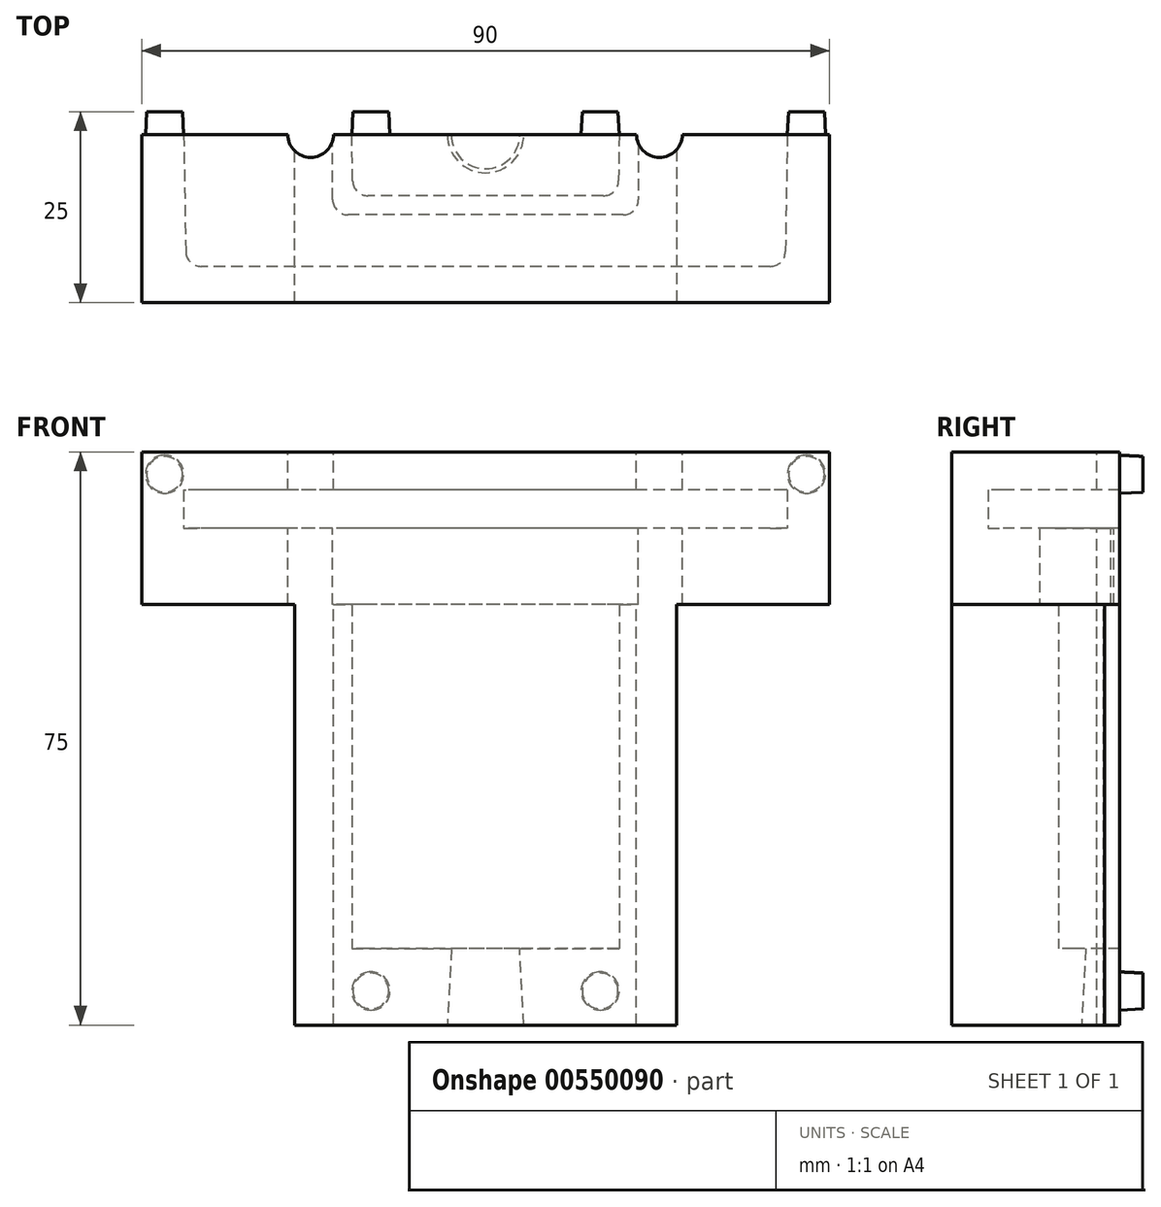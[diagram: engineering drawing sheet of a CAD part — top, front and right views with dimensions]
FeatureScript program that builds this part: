
annotation { "Feature Type Name" : "Feature", "Feature Type Description" : "" }
export const myFeature = defineFeature(function(context is Context, id is Id, definition is map)
    precondition{}
    {
        {
            var Q0;
            Q0=qCreatedBy(makeId("Top.planeOp"),FACE);
            var sketch = newSketch(context, id + "F0", { "sketchPlane" : qUnion([Q0])});
            skLineSegment(sketch, "E0.bottom", {"start": v(45, -44.53) * mm, "end": v(-45, -44.53) * mm});
            skLineSegment(sketch, "E0.top", {"start": v(45, -66.53) * mm, "end": v(-45, -66.53) * mm});
            skLineSegment(sketch, "E0.left", {"start": v(45, -44.53) * mm, "end": v(45, -66.53) * mm});
            skLineSegment(sketch, "E0.right", {"start": v(-45, -44.53) * mm, "end": v(-45, -66.53) * mm});
            skPoint(sketch, "E0.middle", {"position": v(0, -55.53) * mm});
            skSolve(sketch);
        }
        {
            var Q0;
            Q0 = qSketchRegion(id + "F0", true);
            extrude(context, id + "F1", {"entities" : qUnion([Q0]), "depth" : 10 * mm, "offsetDistance" : 25 * mm});
        }
        {
            var Q0;
            Q0=makeQuery(id+"F1.opExtrude","CAP_FACE",FACE,{"disambiguationData":[OSD([sQuery(id+"F0.wireOp",EDGE,"E0.bottom"),sQuery(id+"F0.wireOp",EDGE,"E0.top"),sQuery(id+"F0.wireOp",EDGE,"E0.left"),sQuery(id+"F0.wireOp",EDGE,"E0.right")])],"isStart":true});
            var sketch = newSketch(context, id + "F2", { "sketchPlane" : qUnion([Q0])});
            skLineSegment(sketch, "E1", {"start": v(0, 44.53) * mm, "end": v(39.5, 44.53) * mm});
            skLineSegment(sketch, "E2", {"start": v(39.5, 44.53) * mm, "end": v(39.5, 61.78) * mm});
            skLineSegment(sketch, "E3", {"start": v(39.5, 61.78) * mm, "end": v(-39.5, 61.78) * mm});
            skLineSegment(sketch, "E4", {"start": v(-39.5, 61.78) * mm, "end": v(-39.5, 44.53) * mm});
            skLineSegment(sketch, "E5", {"start": v(-39.5, 44.53) * mm, "end": v(0, 44.53) * mm});
            skLineSegment(sketch, "E6", {"start": v(-39.5, 44.53) * mm, "end": v(-39.2, 61.78) * mm});
            skLineSegment(sketch, "E7", {"start": v(39.5, 44.53) * mm, "end": v(39.2, 61.78) * mm});
            skSolve(sketch);
        }
        {
            var Q0;
            Q0=makeQuery(id+"F2.imprint","IMPRINT",FACE,{"disambiguationData":[TD([[makeQuery(id+"F2.imprint","IMPRINT",EDGE,{"derivedFrom":sQuery(id+"F2.wireOp",EDGE,"E1")}),-1.0]])]});
            extrude(context, id + "F3", {"entities" : qUnion([Q0]), "operationType" : NewBodyOperationType.REMOVE, "oppositeDirection" : true, "depth" : 5 * mm, "offsetDistance" : 25 * mm});
        }
        {
            var Q0;
            Q0=makeQuery(id+"F3.boolean.opBoolean","COPY",EDGE,{"derivedFrom":makeQuery(id+"F3.opExtrude","SWEPT_EDGE",EDGE,{"disambiguationData":[OSD([sQuery(id+"F2.wireOp",EDGE,"E3"),sQuery(id+"F2.wireOp",EDGE,"E6")])]})});
            var Q1;
            Q1=makeQuery(id+"F3.boolean.opBoolean","COPY",EDGE,{"derivedFrom":makeQuery(id+"F3.opExtrude","SWEPT_EDGE",EDGE,{"disambiguationData":[OSD([sQuery(id+"F2.wireOp",EDGE,"E3"),sQuery(id+"F2.wireOp",EDGE,"E7")])]})});
            fillet(context, id + "F4", {"entities" : qUnion([Q0, Q1]), "radius" : 2 * mm, "tangentPropagation" : true, "allowEdgeOverflow" : false});
        }
        {
            var Q0;
            Q0=makeQuery(id+"F1.opExtrude","CAP_FACE",FACE,{"disambiguationData":[OSD([sQuery(id+"F0.wireOp",EDGE,"E0.bottom"),sQuery(id+"F0.wireOp",EDGE,"E0.top"),sQuery(id+"F0.wireOp",EDGE,"E0.left"),sQuery(id+"F0.wireOp",EDGE,"E0.right")])],"isStart":true});
            var sketch = newSketch(context, id + "F5", { "sketchPlane" : qUnion([Q0])});
            skLineSegment(sketch, "E8", {"start": v(-45, 44.53) * mm, "end": v(45, 44.53) * mm});
            skLineSegment(sketch, "E9", {"start": v(45, 44.53) * mm, "end": v(45, 66.53) * mm});
            skLineSegment(sketch, "E10", {"start": v(45, 66.53) * mm, "end": v(-45, 66.53) * mm});
            skLineSegment(sketch, "E11", {"start": v(-45, 66.53) * mm, "end": v(-45, 44.53) * mm});
            skSolve(sketch);
        }
        {
            var Q0;
            Q0 = qSketchRegion(id + "F5", true);
            extrude(context, id + "F6", {"entities" : qUnion([Q0]), "operationType" : NewBodyOperationType.ADD, "depth" : 10 * mm, "offsetDistance" : 25 * mm});
        }
        {
            var Q0;
            Q0=makeQuery(id+"F6.opExtrude","CAP_FACE",FACE,{"disambiguationData":[OSD([sQuery(id+"F5.wireOp",EDGE,"E8"),sQuery(id+"F5.wireOp",EDGE,"E9"),sQuery(id+"F5.wireOp",EDGE,"E10"),sQuery(id+"F5.wireOp",EDGE,"E11")])],"isStart":false});
            var sketch = newSketch(context, id + "F7", { "sketchPlane" : qUnion([Q0])});
            skLineSegment(sketch, "E12", {"start": v(0, 44.53) * mm, "end": v(20, 44.53) * mm});
            skLineSegment(sketch, "E13", {"start": v(20, 44.53) * mm, "end": v(20, 55.03) * mm});
            skLineSegment(sketch, "E14", {"start": v(20, 55.03) * mm, "end": v(-20, 55.03) * mm});
            skLineSegment(sketch, "E15", {"start": v(-20, 55.03) * mm, "end": v(-20, 44.53) * mm});
            skLineSegment(sketch, "E16", {"start": v(-20, 44.53) * mm, "end": v(0, 44.53) * mm});
            skLineSegment(sketch, "E17", {"start": v(-20, 44.53) * mm, "end": v(-19.82, 55.03) * mm});
            skLineSegment(sketch, "E18", {"start": v(20, 44.53) * mm, "end": v(19.82, 55.03) * mm});
            skSolve(sketch);
        }
        {
            var Q0;
            Q0 = qSketchRegion(id + "F7", true);
            var Q1;
            Q1=makeQuery(id+"F7.imprint","IMPRINT",FACE,{"disambiguationData":[TD([[makeQuery(id+"F7.imprint","IMPRINT",EDGE,{"derivedFrom":sQuery(id+"F7.wireOp",EDGE,"E12")}),-1.0]])]});
            extrude(context, id + "F8", {"entities" : qUnion([Q0, Q1]), "operationType" : NewBodyOperationType.REMOVE, "oppositeDirection" : true, "depth" : 10 * mm, "offsetDistance" : 25 * mm});
        }
        {
            var Q0;
            Q0=makeQuery(id+"F8.boolean.opBoolean","COPY",EDGE,{"derivedFrom":makeQuery(id+"F8.opExtrude","SWEPT_EDGE",EDGE,{"disambiguationData":[OSD([sQuery(id+"F7.wireOp",EDGE,"E14"),sQuery(id+"F7.wireOp",EDGE,"E15")])]})});
            var Q1;
            Q1=makeQuery(id+"F8.boolean.opBoolean","COPY",EDGE,{"derivedFrom":makeQuery(id+"F8.opExtrude","SWEPT_EDGE",EDGE,{"disambiguationData":[OSD([sQuery(id+"F7.wireOp",EDGE,"E13"),sQuery(id+"F7.wireOp",EDGE,"E14")])]})});
            fillet(context, id + "F9", {"entities" : qUnion([Q0, Q1]), "radius" : 2 * mm, "tangentPropagation" : true, "allowEdgeOverflow" : false});
        }
        {
            var Q0;
            Q0=makeQuery(id+"F6.opExtrude","CAP_FACE",FACE,{"disambiguationData":[OSD([sQuery(id+"F5.wireOp",EDGE,"E8"),sQuery(id+"F5.wireOp",EDGE,"E9"),sQuery(id+"F5.wireOp",EDGE,"E10"),sQuery(id+"F5.wireOp",EDGE,"E11")])],"isStart":false});
            var sketch = newSketch(context, id + "F10", { "sketchPlane" : qUnion([Q0])});
            skLineSegment(sketch, "E19", {"start": v(0, 44.53) * mm, "end": v(25, 44.53) * mm});
            skLineSegment(sketch, "E20", {"start": v(25, 44.53) * mm, "end": v(25, 66.53) * mm});
            skLineSegment(sketch, "E21", {"start": v(25, 66.53) * mm, "end": v(-25, 66.53) * mm});
            skLineSegment(sketch, "E22", {"start": v(-25, 66.53) * mm, "end": v(-25, 44.53) * mm});
            skLineSegment(sketch, "E23", {"start": v(-25, 44.53) * mm, "end": v(0, 44.53) * mm});
            skSolve(sketch);
        }
        {
            var Q0;
            Q0 = qSketchRegion(id + "F10", true);
            extrude(context, id + "F11", {"entities" : qUnion([Q0]), "operationType" : NewBodyOperationType.ADD, "depth" : 45 * mm, "offsetDistance" : 25 * mm});
        }
        {
            var Q0;
            Q0=makeQuery(id+"F11.opExtrude","CAP_FACE",FACE,{"disambiguationData":[OSD([sQuery(id+"F10.wireOp",EDGE,"E19"),sQuery(id+"F10.wireOp",EDGE,"E20"),sQuery(id+"F10.wireOp",EDGE,"E21"),sQuery(id+"F10.wireOp",EDGE,"E22"),sQuery(id+"F10.wireOp",EDGE,"E23")])],"isStart":false});
            var sketch = newSketch(context, id + "F12", { "sketchPlane" : qUnion([Q0])});
            skLineSegment(sketch, "E24", {"start": v(0, 44.53) * mm, "end": v(17.5, 44.53) * mm});
            skLineSegment(sketch, "E25", {"start": v(17.5, 44.53) * mm, "end": v(17.5, 52.53) * mm});
            skLineSegment(sketch, "E26", {"start": v(17.5, 52.53) * mm, "end": v(-17.5, 52.53) * mm});
            skLineSegment(sketch, "E27", {"start": v(-17.5, 52.53) * mm, "end": v(-17.5, 44.53) * mm});
            skLineSegment(sketch, "E28", {"start": v(-17.5, 44.53) * mm, "end": v(0, 44.53) * mm});
            skLineSegment(sketch, "E29", {"start": v(-17.36, 52.53) * mm, "end": v(-17.5, 44.53) * mm});
            skLineSegment(sketch, "E30", {"start": v(17.5, 44.53) * mm, "end": v(17.36, 52.53) * mm});
            skSolve(sketch);
        }
        {
            var Q0;
            Q0=makeQuery(id+"F12.imprint","IMPRINT",FACE,{"disambiguationData":[TD([[makeQuery(id+"F12.imprint","IMPRINT",EDGE,{"derivedFrom":sQuery(id+"F12.wireOp",EDGE,"E24")}),1.0]])]});
            extrude(context, id + "F13", {"entities" : qUnion([Q0]), "operationType" : NewBodyOperationType.REMOVE, "oppositeDirection" : true, "depth" : 45 * mm, "offsetDistance" : 25 * mm});
        }
        {
            var Q0;
            Q0=makeQuery(id+"F13.boolean.opBoolean","COPY",EDGE,{"derivedFrom":makeQuery(id+"F13.opExtrude","SWEPT_EDGE",EDGE,{"disambiguationData":[OSD([sQuery(id+"F12.wireOp",EDGE,"E26"),sQuery(id+"F12.wireOp",EDGE,"E29")])]})});
            var Q1;
            Q1=makeQuery(id+"F13.boolean.opBoolean","COPY",EDGE,{"derivedFrom":makeQuery(id+"F13.opExtrude","SWEPT_EDGE",EDGE,{"disambiguationData":[OSD([sQuery(id+"F12.wireOp",EDGE,"E26"),sQuery(id+"F12.wireOp",EDGE,"E30")])]})});
            fillet(context, id + "F14", {"entities" : qUnion([Q0, Q1]), "radius" : 2 * mm, "tangentPropagation" : true, "allowEdgeOverflow" : false});
        }
        {
            var Q0;
            Q0=makeQuery(id+"F11.opExtrude","CAP_FACE",FACE,{"disambiguationData":[OSD([sQuery(id+"F10.wireOp",EDGE,"E19"),sQuery(id+"F10.wireOp",EDGE,"E20"),sQuery(id+"F10.wireOp",EDGE,"E21"),sQuery(id+"F10.wireOp",EDGE,"E22"),sQuery(id+"F10.wireOp",EDGE,"E23")])],"isStart":false});
            var sketch = newSketch(context, id + "F15", { "sketchPlane" : qUnion([Q0])});
            skLineSegment(sketch, "E31.bottom", {"start": v(-25, 66.53) * mm, "end": v(25, 66.53) * mm});
            skLineSegment(sketch, "E31.top", {"start": v(-25, 44.53) * mm, "end": v(25, 44.53) * mm});
            skLineSegment(sketch, "E31.left", {"start": v(-25, 66.53) * mm, "end": v(-25, 44.53) * mm});
            skLineSegment(sketch, "E31.right", {"start": v(25, 66.53) * mm, "end": v(25, 44.53) * mm});
            skSolve(sketch);
        }
        {
            var Q0;
            Q0 = qSketchRegion(id + "F15", true);
            extrude(context, id + "F16", {"entities" : qUnion([Q0]), "operationType" : NewBodyOperationType.ADD, "depth" : 10 * mm, "offsetDistance" : 25 * mm});
        }
        {
            var Q0;
            Q0=makeQuery(id+"F16.opExtrude","CAP_FACE",FACE,{"disambiguationData":[OSD([sQuery(id+"F15.wireOp",EDGE,"E31.bottom"),sQuery(id+"F15.wireOp",EDGE,"E31.top"),sQuery(id+"F15.wireOp",EDGE,"E31.left"),sQuery(id+"F15.wireOp",EDGE,"E31.right")])],"isStart":false});
            var sketch = newSketch(context, id + "F17", { "sketchPlane" : qUnion([Q0])});
            skCircle(sketch, "E32", {"center": v(0, 44.53) * mm, "radius": 5 * mm});
            skSolve(sketch);
        }
        {
            var Q0;
            Q0 = qSketchRegion(id + "F17", true);
            extrude(context, id + "F18", {"entities" : qUnion([Q0]), "operationType" : NewBodyOperationType.REMOVE, "oppositeDirection" : true, "depth" : 25 * mm, "offsetDistance" : 25 * mm, "hasDraft" : true, "draftAngle" : 3 * degree, "draftPullDirection" : true});
        }
        {
            var Q0;
            Q0=makeQuery(id+"F1.opExtrude","CAP_FACE",FACE,{"disambiguationData":[OSD([sQuery(id+"F0.wireOp",EDGE,"E0.bottom"),sQuery(id+"F0.wireOp",EDGE,"E0.top"),sQuery(id+"F0.wireOp",EDGE,"E0.left"),sQuery(id+"F0.wireOp",EDGE,"E0.right")])],"isStart":false});
            var sketch = newSketch(context, id + "F19", { "sketchPlane" : qUnion([Q0])});
            skLineSegment(sketch, "E33", {"start": v(0, -44.53) * mm, "end": v(22.8, -44.53) * mm});
            skLineSegment(sketch, "E34", {"start": v(0, -44.53) * mm, "end": v(-22.8, -44.53) * mm});
            skSolve(sketch);
        }
        {
            var Q0;
            {var subQ2=sQuery(id+"F19.wireOp",EDGE,"E33");Q0=makeQuery(id+"F19.imprint","IMPRINT",FACE,{"disambiguationData":[TD([[makeQuery(id+"F19.imprint","IMPRINT",EDGE,{"derivedFrom":subQ2}),1.0]])]});}
            var sketch = newSketch(context, id + "F20", { "sketchPlane" : qUnion([Q0])});
            skCircle(sketch, "E35", {"center": v(22.75, -44.52) * mm, "radius": 3 * mm});
            skCircle(sketch, "E36", {"center": v(-22.89, -44.52) * mm, "radius": 3 * mm});
            skSolve(sketch);
        }
        {
            var Q0;
            Q0 = qSketchRegion(id + "F20", true);
            extrude(context, id + "F21", {"entities" : qUnion([Q0]), "operationType" : NewBodyOperationType.REMOVE, "oppositeDirection" : true, "depth" : 90 * mm, "offsetDistance" : 25 * mm});
        }
        {
            var Q0;
            {var subQ0=sQuery(id+"F15.wireOp",EDGE,"E31.right");var subQ1=sQuery(id+"F15.wireOp",EDGE,"E31.left");var subQ2=sQuery(id+"F15.wireOp",EDGE,"E31.top");var subQ3=sQuery(id+"F15.wireOp",EDGE,"E31.bottom");var subQ4=sQuery(id+"F10.wireOp",EDGE,"E23");var subQ5=sQuery(id+"F10.wireOp",EDGE,"E19");Q0=makeQuery(id+"F21.boolean.opBoolean","SPLIT",FACE,{"disambiguationData":[TD([makeQuery(id+"F11.opExtrude","CAP_FACE",FACE,{"disambiguationData":[OSD([subQ5,sQuery(id+"F10.wireOp",EDGE,"E20"),sQuery(id+"F10.wireOp",EDGE,"E21"),sQuery(id+"F10.wireOp",EDGE,"E22"),subQ4])],"isStart":true}),makeQuery(id+"F13.boolean.opBoolean","COPY",FACE,{"derivedFrom":makeQuery(id+"F13.opExtrude","SWEPT_FACE",FACE,{"disambiguationData":[OSD([sQuery(id+"F12.wireOp",EDGE,"E30")])]})}),makeQuery(id+"F16.opExtrude","CAP_FACE",FACE,{"disambiguationData":[OSD([subQ3,subQ2,subQ1,subQ0])],"isStart":true}),makeQuery(id+"F16.opExtrude","CAP_FACE",FACE,{"disambiguationData":[OSD([subQ3,subQ2,subQ1,subQ0])],"isStart":false}),makeQuery(id+"F18.boolean.opBoolean","COPY",FACE,{"derivedFrom":makeQuery(id+"F18.opExtrude","SWEPT_FACE",FACE,{"disambiguationData":[OSD([sQuery(id+"F17.wireOp",EDGE,"E32")])]})}),makeQuery(id+"F21.opExtrude","SWEPT_FACE",FACE,{"disambiguationData":[OSD([sQuery(id+"F20.wireOp",EDGE,"E35")])]})])],"derivedFrom":makeQuery(id+"F16.boolean.opBoolean","MERGE",FACE,{"derivedFrom":[makeQuery(id+"F11.boolean.opBoolean","MERGE",FACE,{"derivedFrom":[makeQuery(id+"F6.boolean.opBoolean","MERGE",FACE,{"derivedFrom":[makeQuery(id+"F1.opExtrude","SWEPT_FACE",FACE,{"disambiguationData":[OSD([sQuery(id+"F0.wireOp",EDGE,"E0.bottom")])]}),makeQuery(id+"F6.opExtrude","SWEPT_FACE",FACE,{"disambiguationData":[OSD([sQuery(id+"F5.wireOp",EDGE,"E8")])]})]}),makeQuery(id+"F11.opExtrude","SWEPT_FACE",FACE,{"disambiguationData":[OSD([subQ5,subQ4])]})]}),makeQuery(id+"F16.opExtrude","SWEPT_FACE",FACE,{"disambiguationData":[OSD([subQ2])]})]})});}
            var sketch = newSketch(context, id + "F22", { "sketchPlane" : qUnion([Q0])});
            skCircle(sketch, "E37", {"center": v(-15, -60.54) * mm, "radius": 2.5 * mm});
            skCircle(sketch, "E38.MirrorC", {"center": v(15, -60.54) * mm, "radius": 2.5 * mm});
            skSolve(sketch);
        }
        {
            var Q0;
            Q0 = qSketchRegion(id + "F22", true);
            extrude(context, id + "F23", {"entities" : qUnion([Q0]), "operationType" : NewBodyOperationType.ADD, "depth" : 3 * mm, "offsetDistance" : 25 * mm, "hasDraft" : true, "draftAngle" : 3 * degree, "draftPullDirection" : true});
        }
        {
            var Q0;
            {var subQ0=sQuery(id+"F2.wireOp",EDGE,"E7");var subQ1=sQuery(id+"F0.wireOp",EDGE,"E0.left");var subQ2=sQuery(id+"F0.wireOp",EDGE,"E0.bottom");var subQ3=sQuery(id+"F5.wireOp",EDGE,"E9");var subQ4=sQuery(id+"F5.wireOp",EDGE,"E11");var subQ5=sQuery(id+"F5.wireOp",EDGE,"E10");var subQ6=sQuery(id+"F5.wireOp",EDGE,"E8");Q0=makeQuery(id+"F21.boolean.opBoolean","SPLIT",FACE,{"disambiguationData":[TD([makeQuery(id+"F1.opExtrude","CAP_FACE",FACE,{"disambiguationData":[OSD([subQ2,sQuery(id+"F0.wireOp",EDGE,"E0.top"),subQ1,sQuery(id+"F0.wireOp",EDGE,"E0.right")])],"isStart":false}),makeQuery(id+"F1.opExtrude","SWEPT_FACE",FACE,{"disambiguationData":[OSD([subQ1])]}),makeQuery(id+"F3.boolean.opBoolean","COPY",FACE,{"derivedFrom":makeQuery(id+"F3.opExtrude","CAP_FACE",FACE,{"disambiguationData":[OSD([sQuery(id+"F2.wireOp",EDGE,"E1"),sQuery(id+"F2.wireOp",EDGE,"E3"),sQuery(id+"F2.wireOp",EDGE,"E5"),sQuery(id+"F2.wireOp",EDGE,"E6"),subQ0])],"isStart":false})}),makeQuery(id+"F3.boolean.opBoolean","COPY",FACE,{"derivedFrom":makeQuery(id+"F3.opExtrude","SWEPT_FACE",FACE,{"disambiguationData":[OSD([subQ0])]})}),makeQuery(id+"F6.opExtrude","CAP_FACE",FACE,{"disambiguationData":[OSD([subQ6,subQ3,subQ5,subQ4])],"isStart":true}),makeQuery(id+"F6.opExtrude","CAP_FACE",FACE,{"disambiguationData":[OSD([subQ6,subQ3,subQ5,subQ4])],"isStart":false}),makeQuery(id+"F6.opExtrude","SWEPT_FACE",FACE,{"disambiguationData":[OSD([subQ3])]}),makeQuery(id+"F21.opExtrude","SWEPT_FACE",FACE,{"disambiguationData":[OSD([sQuery(id+"F20.wireOp",EDGE,"E35")])]})])],"derivedFrom":makeQuery(id+"F16.boolean.opBoolean","MERGE",FACE,{"derivedFrom":[makeQuery(id+"F11.boolean.opBoolean","MERGE",FACE,{"derivedFrom":[makeQuery(id+"F6.boolean.opBoolean","MERGE",FACE,{"derivedFrom":[makeQuery(id+"F1.opExtrude","SWEPT_FACE",FACE,{"disambiguationData":[OSD([subQ2])]}),makeQuery(id+"F6.opExtrude","SWEPT_FACE",FACE,{"disambiguationData":[OSD([subQ6])]})]}),makeQuery(id+"F11.opExtrude","SWEPT_FACE",FACE,{"disambiguationData":[OSD([sQuery(id+"F10.wireOp",EDGE,"E19"),sQuery(id+"F10.wireOp",EDGE,"E23")])]})]}),makeQuery(id+"F16.opExtrude","SWEPT_FACE",FACE,{"disambiguationData":[OSD([sQuery(id+"F15.wireOp",EDGE,"E31.top")])]})]})});}
            var sketch = newSketch(context, id + "F24", { "sketchPlane" : qUnion([Q0])});
            skCircle(sketch, "E39", {"center": v(-42, 7.06) * mm, "radius": 2.5 * mm});
            skCircle(sketch, "E40.MirrorC", {"center": v(42, 7.06) * mm, "radius": 2.5 * mm});
            skSolve(sketch);
        }
        {
            var Q0;
            Q0 = qSketchRegion(id + "F24", true);
            extrude(context, id + "F25", {"entities" : qUnion([Q0]), "operationType" : NewBodyOperationType.ADD, "depth" : 3 * mm, "offsetDistance" : 25 * mm, "hasDraft" : true, "draftAngle" : 3 * degree, "draftPullDirection" : true});
        }
    });
